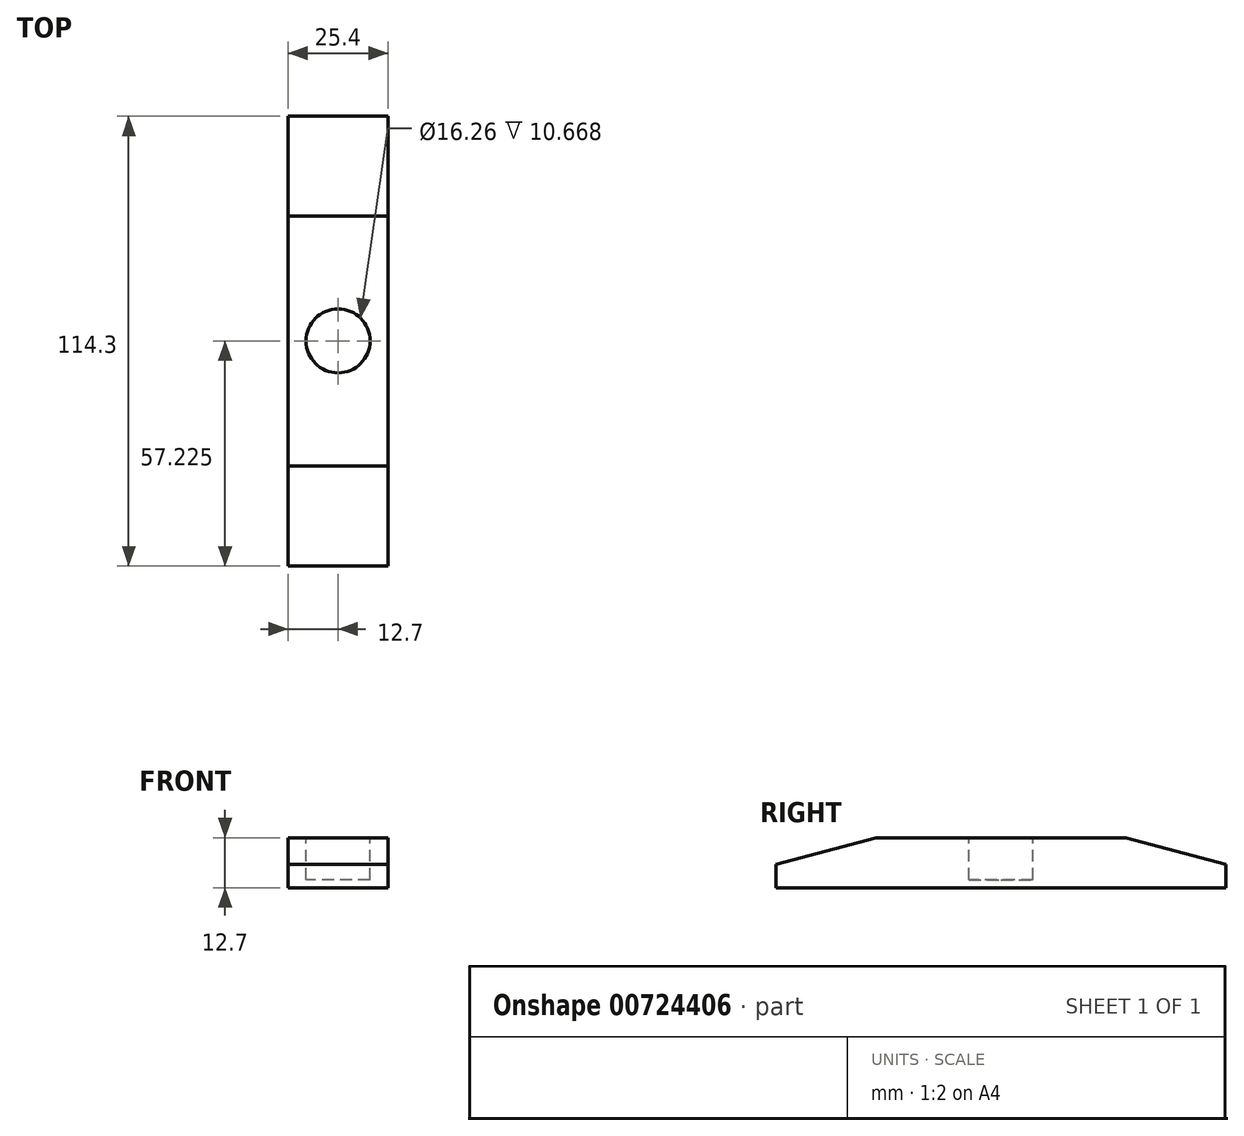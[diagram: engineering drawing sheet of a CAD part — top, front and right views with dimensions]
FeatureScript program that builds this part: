
annotation { "Feature Type Name" : "Feature", "Feature Type Description" : "" }
export const myFeature = defineFeature(function(context is Context, id is Id, definition is map)
    precondition{}
    {
        {
            var Q0;
            Q0=qCreatedBy(makeId("Top.planeOp"),FACE);
            var sketch = newSketch(context, id + "F0", { "sketchPlane" : qUnion([Q0])});
            skLineSegment(sketch, "E0.bottom", {"start": v(12.7, 57.15) * mm, "end": v(-12.7, 57.15) * mm});
            skLineSegment(sketch, "E0.top", {"start": v(12.7, -57.15) * mm, "end": v(-12.7, -57.15) * mm});
            skLineSegment(sketch, "E0.left", {"start": v(12.7, 57.15) * mm, "end": v(12.7, -57.15) * mm});
            skLineSegment(sketch, "E0.right", {"start": v(-12.7, 57.15) * mm, "end": v(-12.7, -57.15) * mm});
            skPoint(sketch, "E0.middle", {"position": v(0, 0) * mm});
            skSolve(sketch);
        }
        {
            var Q0;
            Q0=makeQuery(id+"F0.imprint","IMPRINT",FACE,{"disambiguationData":[TD([[makeQuery(id+"F0.imprint","IMPRINT",EDGE,{"derivedFrom":sQuery(id+"F0.wireOp",EDGE,"E0.bottom")}),1.0]])]});
            extrude(context, id + "F1", {"entities" : qUnion([Q0]), "depth" : 12.7 * mm, "offsetDistance" : 25.4 * mm});
        }
        {
            var Q0;
            Q0=makeQuery(id+"F1.opExtrude","CAP_FACE",FACE,{"disambiguationData":[OSD([sQuery(id+"F0.wireOp",EDGE,"E0.bottom"),sQuery(id+"F0.wireOp",EDGE,"E0.top"),sQuery(id+"F0.wireOp",EDGE,"E0.left"),sQuery(id+"F0.wireOp",EDGE,"E0.right")])],"isStart":false});
            var sketch = newSketch(context, id + "F2", { "sketchPlane" : qUnion([Q0])});
            skCircle(sketch, "E1", {"center": v(0, 0.07) * mm, "radius": 8.13 * mm});
            skSolve(sketch);
        }
        {
            var Q0;
            Q0=makeQuery(id+"F2.imprint","IMPRINT",FACE,{"disambiguationData":[TD([[makeQuery(id+"F2.imprint","IMPRINT",EDGE,{"derivedFrom":sQuery(id+"F2.wireOp",EDGE,"E1")}),1.0]])]});
            extrude(context, id + "F3", {"entities" : qUnion([Q0]), "operationType" : NewBodyOperationType.REMOVE, "oppositeDirection" : true, "depth" : 10.67 * mm, "offsetDistance" : 25.4 * mm});
        }
        {
            var Q0;
            Q0=makeQuery(id+"F1.opExtrude","CAP_EDGE",EDGE,{"disambiguationData":[OSD([sQuery(id+"F0.wireOp",EDGE,"E0.bottom")])],"isStart":false});
            chamfer(context, id + "F4", {"entities" : qUnion([Q0]), "chamferType" : ChamferType.OFFSET_ANGLE, "width" : 25.4 * mm, "oppositeDirection" : false, "angle" : 15 * degree, "tangentPropagation" : true});
        }
        {
            var Q0;
            Q0=makeQuery(id+"F1.opExtrude","CAP_EDGE",EDGE,{"disambiguationData":[OSD([sQuery(id+"F0.wireOp",EDGE,"E0.top")])],"isStart":false});
            chamfer(context, id + "F5", {"entities" : qUnion([Q0]), "chamferType" : ChamferType.OFFSET_ANGLE, "width" : 25.4 * mm, "oppositeDirection" : true, "angle" : 15 * degree, "tangentPropagation" : true});
        }
    });
